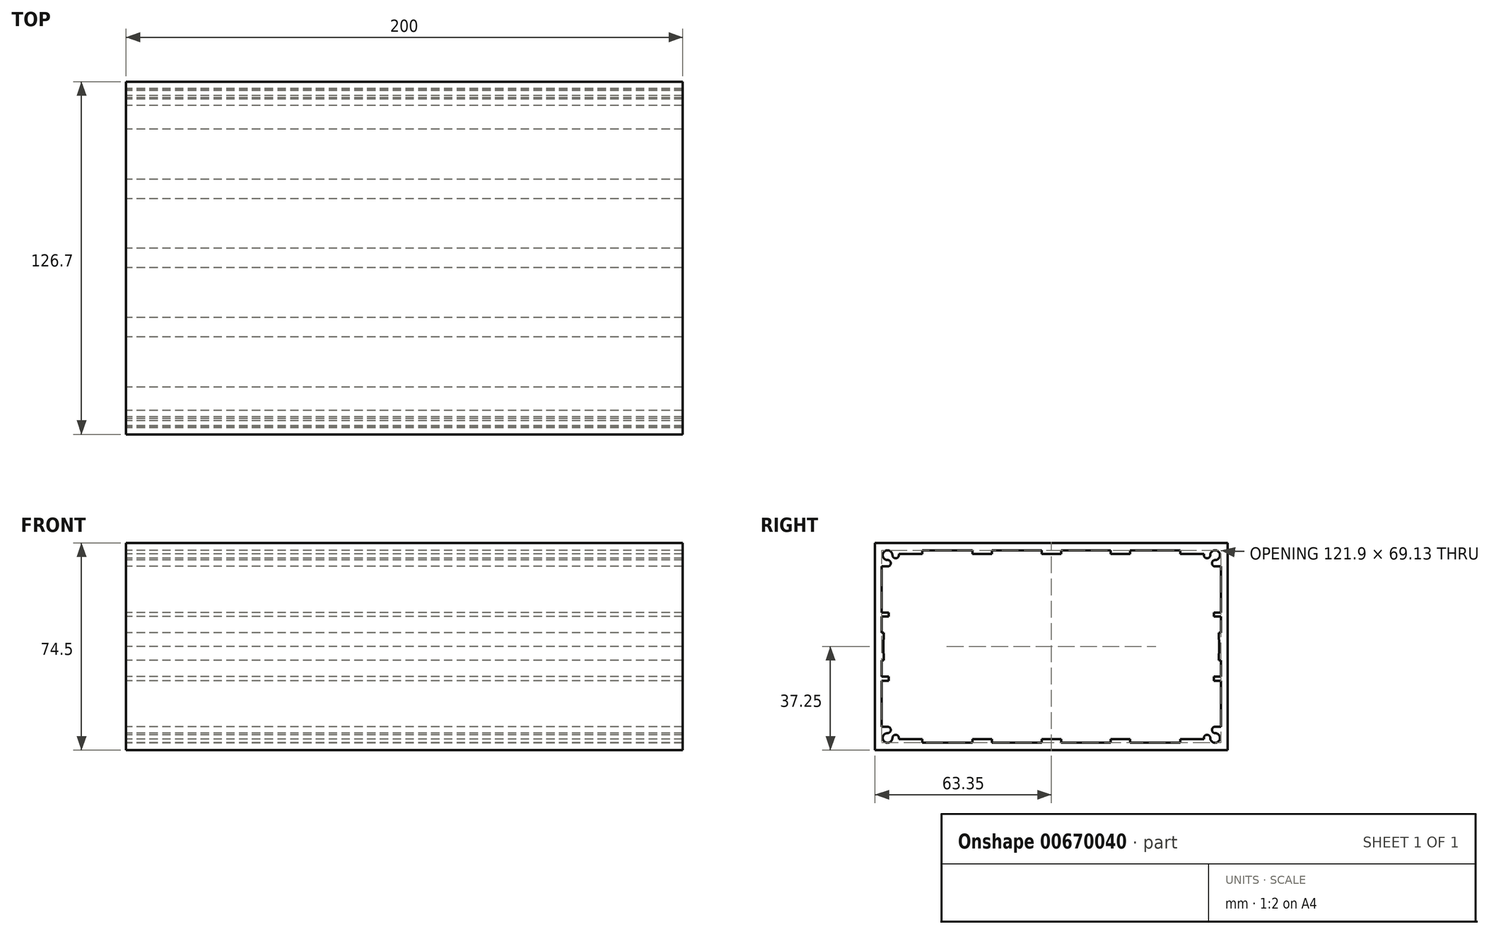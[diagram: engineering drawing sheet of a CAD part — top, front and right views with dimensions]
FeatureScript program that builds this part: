
annotation { "Feature Type Name" : "Feature", "Feature Type Description" : "" }
export const myFeature = defineFeature(function(context is Context, id is Id, definition is map)
    precondition{}
    {
        {
            var Q0;
            Q0=qCreatedBy(makeId("Right.planeOp"),FACE);
            var sketch = newSketch(context, id + "F0", { "sketchPlane" : qUnion([Q0])});
            skLineSegment(sketch, "E0.bottom", {"start": v(0, 0) * mm, "end": v(126.7, 0) * mm});
            skLineSegment(sketch, "E0.top", {"start": v(0, 74.5) * mm, "end": v(126.7, 74.5) * mm});
            skLineSegment(sketch, "E0.left", {"start": v(0, 0) * mm, "end": v(0, 74.5) * mm});
            skLineSegment(sketch, "E0.right", {"start": v(126.7, 0) * mm, "end": v(126.7, 74.5) * mm});
            skLineSegment(sketch, "E1", {"start": v(63.35, 74.5) * mm, "end": v(63.35, 0) * mm, "construction": true});
            skLineSegment(sketch, "E2", {"start": v(0, 37.25) * mm, "end": v(126.7, 37.25) * mm, "construction": true});
            skPoint(sketch, "E3.middle", {"position": v(63.35, 37.25) * mm});
            skLineSegment(sketch, "E4", {"start": v(63.35, 70.5) * mm, "end": v(59.85, 70.5) * mm});
            skLineSegment(sketch, "E5", {"start": v(59.85, 70.5) * mm, "end": v(59.85, 71.8) * mm});
            skLineSegment(sketch, "E6", {"start": v(59.85, 71.8) * mm, "end": v(42, 71.8) * mm});
            skLineSegment(sketch, "E7", {"start": v(42, 71.8) * mm, "end": v(42, 70.5) * mm});
            skLineSegment(sketch, "E8", {"start": v(42, 70.5) * mm, "end": v(35, 70.5) * mm});
            skLineSegment(sketch, "E9", {"start": v(35, 70.5) * mm, "end": v(35, 71.8) * mm});
            skLineSegment(sketch, "E10", {"start": v(35, 71.8) * mm, "end": v(17, 71.8) * mm});
            skLineSegment(sketch, "E11", {"start": v(17, 71.8) * mm, "end": v(17, 70.5) * mm});
            skLineSegment(sketch, "E12", {"start": v(17, 70.5) * mm, "end": v(8.55, 70.5) * mm});
            skArc(sketch, "E13", {"start": v(6.25, 70.1) * mm, "mid": v(3.26, 71.34) * mm, "end": v(4.5, 68.35) * mm});
            skArc(sketch, "E14", {"start": v(6.25, 70.1) * mm, "mid": v(7.4, 68.95) * mm, "end": v(8.55, 70.1) * mm});
            skLineSegment(sketch, "E15", {"start": v(8.55, 70.1) * mm, "end": v(8.55, 70.5) * mm});
            skArc(sketch, "E16", {"start": v(4.5, 66.05) * mm, "mid": v(5.65, 67.2) * mm, "end": v(4.5, 68.35) * mm});
            skLineSegment(sketch, "E17", {"start": v(4.5, 66.05) * mm, "end": v(2.4, 66.05) * mm});
            skLineSegment(sketch, "E18", {"start": v(2.4, 66.05) * mm, "end": v(2.4, 49.5) * mm});
            skLineSegment(sketch, "E19", {"start": v(2.4, 49.5) * mm, "end": v(4.92, 49.5) * mm});
            skLineSegment(sketch, "E20", {"start": v(4.92, 49.5) * mm, "end": v(4.92, 48) * mm});
            skLineSegment(sketch, "E21", {"start": v(4.92, 48) * mm, "end": v(2.4, 48) * mm});
            skLineSegment(sketch, "E22", {"start": v(2.4, 48) * mm, "end": v(2.4, 42.22) * mm});
            skLineSegment(sketch, "E23", {"start": v(2.4, 42.22) * mm, "end": v(3.13, 42.22) * mm});
            skLineSegment(sketch, "E24", {"start": v(3.13, 42.22) * mm, "end": v(3, 37.25) * mm});
            skLineSegment(sketch, "E25.MirrorCS", {"start": v(84.7, 71.8) * mm, "end": v(84.7, 70.5) * mm});
            skLineSegment(sketch, "E26.MirrorCS", {"start": v(124.3, 42.22) * mm, "end": v(123.57, 42.22) * mm});
            skLineSegment(sketch, "E27.MirrorCS", {"start": v(91.7, 70.5) * mm, "end": v(91.7, 71.8) * mm});
            skLineSegment(sketch, "E28.MirrorCS", {"start": v(109.7, 71.8) * mm, "end": v(109.7, 70.5) * mm});
            skLineSegment(sketch, "E29.MirrorCS", {"start": v(121.78, 48) * mm, "end": v(124.3, 48) * mm});
            skLineSegment(sketch, "E30.MirrorCS", {"start": v(121.78, 49.5) * mm, "end": v(121.78, 48) * mm});
            skLineSegment(sketch, "E31.MirrorCS", {"start": v(66.85, 70.5) * mm, "end": v(66.85, 71.8) * mm});
            skLineSegment(sketch, "E32.MirrorCS", {"start": v(118.15, 70.1) * mm, "end": v(118.15, 70.5) * mm});
            skLineSegment(sketch, "E33.MirrorCS", {"start": v(124.3, 66.05) * mm, "end": v(124.3, 49.5) * mm});
            skLineSegment(sketch, "E34.MirrorCS", {"start": v(122.2, 66.05) * mm, "end": v(124.3, 66.05) * mm});
            skLineSegment(sketch, "E35.MirrorCS", {"start": v(124.3, 48) * mm, "end": v(124.3, 42.22) * mm});
            skArc(sketch, "E36.MirrorCS", {"start": v(120.45, 70.1) * mm, "mid": v(119.3, 68.95) * mm, "end": v(118.15, 70.1) * mm});
            skLineSegment(sketch, "E37.MirrorCS", {"start": v(124.3, 49.5) * mm, "end": v(121.78, 49.5) * mm});
            skLineSegment(sketch, "E38.MirrorCS", {"start": v(91.7, 71.8) * mm, "end": v(109.7, 71.8) * mm});
            skLineSegment(sketch, "E39.MirrorCS", {"start": v(123.57, 42.22) * mm, "end": v(123.7, 37.25) * mm});
            skLineSegment(sketch, "E40.MirrorCS", {"start": v(109.7, 70.5) * mm, "end": v(118.15, 70.5) * mm});
            skLineSegment(sketch, "E41.MirrorCS", {"start": v(66.85, 71.8) * mm, "end": v(84.7, 71.8) * mm});
            skLineSegment(sketch, "E42.MirrorCS", {"start": v(63.35, 70.5) * mm, "end": v(66.85, 70.5) * mm});
            skLineSegment(sketch, "E43.MirrorCS", {"start": v(84.7, 70.5) * mm, "end": v(91.7, 70.5) * mm});
            skArc(sketch, "E44.MirrorCS", {"start": v(120.45, 70.1) * mm, "mid": v(123.44, 71.34) * mm, "end": v(122.2, 68.35) * mm});
            skArc(sketch, "E45.MirrorCS", {"start": v(122.2, 66.05) * mm, "mid": v(121.05, 67.2) * mm, "end": v(122.2, 68.35) * mm});
            skLineSegment(sketch, "E46.MirrorCS", {"start": v(2.4, 8.45) * mm, "end": v(2.4, 25) * mm});
            skLineSegment(sketch, "E47.MirrorCS", {"start": v(4.5, 8.45) * mm, "end": v(2.4, 8.45) * mm});
            skLineSegment(sketch, "E48.MirrorCS", {"start": v(5, 19.2) * mm, "end": v(5, 19.21) * mm});
            skArc(sketch, "E49.MirrorCS", {"start": v(120.45, 4.4) * mm, "mid": v(119.3, 5.55) * mm, "end": v(118.15, 4.4) * mm});
            skLineSegment(sketch, "E50.MirrorCS", {"start": v(8.55, 4.4) * mm, "end": v(8.55, 4) * mm});
            skLineSegment(sketch, "E51.MirrorCS", {"start": v(118.15, 4.4) * mm, "end": v(118.15, 4) * mm});
            skLineSegment(sketch, "E52.MirrorCS", {"start": v(63.35, 4) * mm, "end": v(59.85, 4) * mm});
            skArc(sketch, "E53.MirrorCS", {"start": v(6.25, 4.4) * mm, "mid": v(7.4, 5.55) * mm, "end": v(8.55, 4.4) * mm});
            skLineSegment(sketch, "E54.MirrorCS", {"start": v(59.85, 4) * mm, "end": v(59.85, 2.7) * mm});
            skLineSegment(sketch, "E55.MirrorCS", {"start": v(124.3, 25) * mm, "end": v(121.78, 25) * mm});
            skLineSegment(sketch, "E56.MirrorCS", {"start": v(4.92, 26.5) * mm, "end": v(2.4, 26.5) * mm});
            skArc(sketch, "E57.MirrorCS", {"start": v(4.5, 8.45) * mm, "mid": v(5.65, 7.3) * mm, "end": v(4.5, 6.15) * mm});
            skLineSegment(sketch, "E58.MirrorCS", {"start": v(121.78, 25) * mm, "end": v(121.78, 26.5) * mm});
            skLineSegment(sketch, "E59.MirrorCS", {"start": v(2.4, 32.28) * mm, "end": v(3.13, 32.28) * mm});
            skLineSegment(sketch, "E60.MirrorCS", {"start": v(4.92, 25) * mm, "end": v(4.92, 26.5) * mm});
            skLineSegment(sketch, "E61.MirrorCS", {"start": v(122.2, 8.45) * mm, "end": v(124.3, 8.45) * mm});
            skLineSegment(sketch, "E62.MirrorCS", {"start": v(121.78, 26.5) * mm, "end": v(124.3, 26.5) * mm});
            skLineSegment(sketch, "E63.MirrorCS", {"start": v(63.35, 4) * mm, "end": v(66.85, 4) * mm});
            skLineSegment(sketch, "E64.MirrorCS", {"start": v(124.3, 8.45) * mm, "end": v(124.3, 25) * mm});
            skLineSegment(sketch, "E65.MirrorCS", {"start": v(2.4, 25) * mm, "end": v(4.92, 25) * mm});
            skLineSegment(sketch, "E66.MirrorCS", {"start": v(109.7, 2.7) * mm, "end": v(109.7, 4) * mm});
            skLineSegment(sketch, "E67.MirrorCS", {"start": v(2.4, 26.5) * mm, "end": v(2.4, 32.28) * mm});
            skLineSegment(sketch, "E68.MirrorCS", {"start": v(84.7, 2.7) * mm, "end": v(84.7, 4) * mm});
            skLineSegment(sketch, "E69.MirrorCS", {"start": v(42, 2.7) * mm, "end": v(42, 4) * mm});
            skLineSegment(sketch, "E70.MirrorCS", {"start": v(124.3, 32.28) * mm, "end": v(123.57, 32.28) * mm});
            skLineSegment(sketch, "E71.MirrorCS", {"start": v(66.85, 4) * mm, "end": v(66.85, 2.7) * mm});
            skLineSegment(sketch, "E72.MirrorCS", {"start": v(17, 2.7) * mm, "end": v(17, 4) * mm});
            skLineSegment(sketch, "E73.MirrorCS", {"start": v(91.7, 4) * mm, "end": v(91.7, 2.7) * mm});
            skLineSegment(sketch, "E74.MirrorCS", {"start": v(124.3, 26.5) * mm, "end": v(124.3, 32.28) * mm});
            skArc(sketch, "E75.MirrorCS", {"start": v(122.2, 8.45) * mm, "mid": v(121.05, 7.3) * mm, "end": v(122.2, 6.15) * mm});
            skLineSegment(sketch, "E76.MirrorCS", {"start": v(35, 4) * mm, "end": v(35, 2.7) * mm});
            skArc(sketch, "E77.MirrorCS", {"start": v(6.25, 4.4) * mm, "mid": v(3.26, 3.16) * mm, "end": v(4.5, 6.15) * mm});
            skArc(sketch, "E78.MirrorCS", {"start": v(120.45, 4.4) * mm, "mid": v(123.44, 3.16) * mm, "end": v(122.2, 6.15) * mm});
            skLineSegment(sketch, "E79.MirrorCS", {"start": v(3.13, 32.28) * mm, "end": v(3, 37.25) * mm});
            skLineSegment(sketch, "E80.MirrorCS", {"start": v(123.57, 32.28) * mm, "end": v(123.7, 37.25) * mm});
            skLineSegment(sketch, "E81.MirrorCS", {"start": v(17, 4) * mm, "end": v(8.55, 4) * mm});
            skLineSegment(sketch, "E82.MirrorCS", {"start": v(109.7, 4) * mm, "end": v(118.15, 4) * mm});
            skLineSegment(sketch, "E83.MirrorCS", {"start": v(84.7, 4) * mm, "end": v(91.7, 4) * mm});
            skLineSegment(sketch, "E84.MirrorCS", {"start": v(66.85, 2.7) * mm, "end": v(84.7, 2.7) * mm});
            skLineSegment(sketch, "E85.MirrorCS", {"start": v(42, 4) * mm, "end": v(35, 4) * mm});
            skLineSegment(sketch, "E86.MirrorCS", {"start": v(35, 2.7) * mm, "end": v(17, 2.7) * mm});
            skLineSegment(sketch, "E87.MirrorCS", {"start": v(91.7, 2.7) * mm, "end": v(109.7, 2.7) * mm});
            skLineSegment(sketch, "E88.MirrorCS", {"start": v(59.85, 2.7) * mm, "end": v(42, 2.7) * mm});
            skSolve(sketch);
        }
        {
            var Q0;
            Q0=qSketchRegion(id+"F0",true);
            extrude(context, id + "F1", {"entities" : qUnion([Q0]), "depth" : 200 * mm, "offsetDistance" : 25 * mm});
        }
    });
